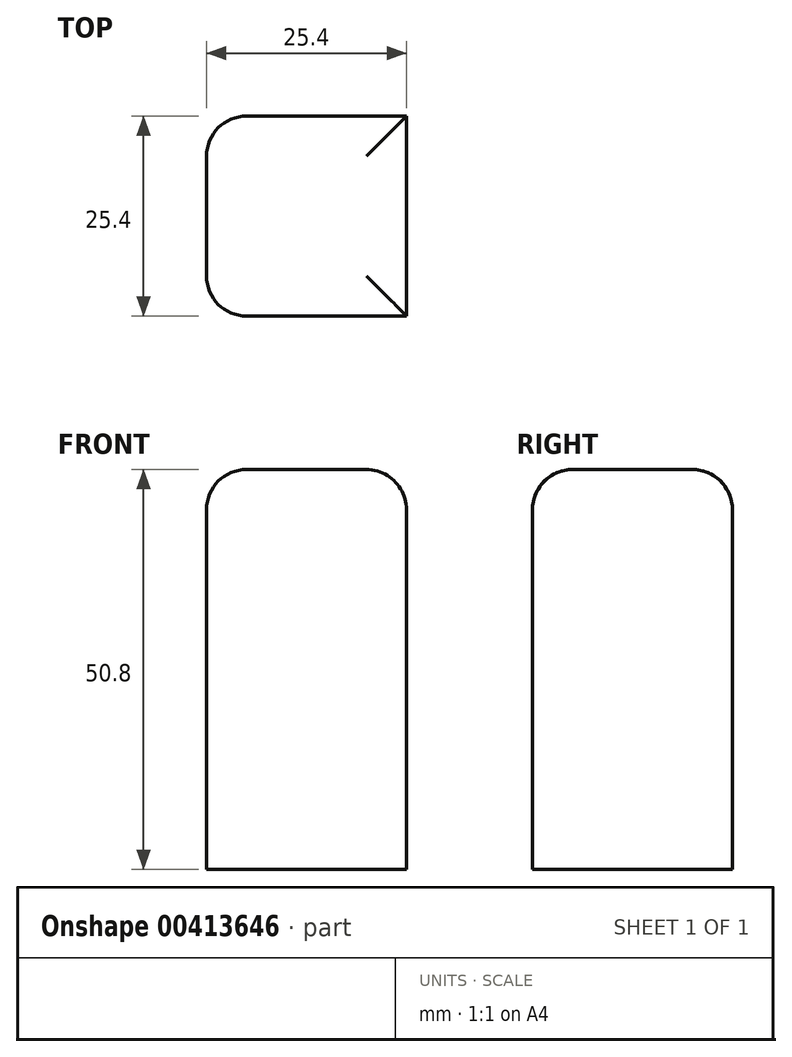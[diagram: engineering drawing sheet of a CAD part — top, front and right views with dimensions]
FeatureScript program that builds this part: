
annotation { "Feature Type Name" : "Feature", "Feature Type Description" : "" }
export const myFeature = defineFeature(function(context is Context, id is Id, definition is map)
    precondition{}
    {
        {
            var Q0;
            Q0=qCreatedBy(makeId("Top.planeOp"),FACE);
            var sketch = newSketch(context, id + "F0", { "sketchPlane" : qUnion([Q0])});
            skLineSegment(sketch, "E0.bottom", {"start": v(-47.8, -39.45) * mm, "end": v(-22.4, -39.45) * mm});
            skLineSegment(sketch, "E0.top", {"start": v(-47.8, -14.05) * mm, "end": v(-22.4, -14.05) * mm});
            skLineSegment(sketch, "E0.left", {"start": v(-47.8, -39.45) * mm, "end": v(-47.8, -14.05) * mm});
            skLineSegment(sketch, "E0.right", {"start": v(-22.4, -39.45) * mm, "end": v(-22.4, -14.05) * mm});
            skSolve(sketch);
        }
        {
            var Q0;
            Q0 = qSketchRegion(id + "F0", true);
            extrude(context, id + "F1", {"entities" : qUnion([Q0]), "depth" : 50.8 * mm});
        }
        {
            var Q0;
            Q0=makeQuery(id+"F1.opExtrude","CAP_EDGE",EDGE,{"disambiguationData":[OSD([sQuery(id+"F0.wireOp",EDGE,"E0.left")])],"isStart":false});
            fillet(context, id + "F2", {"entities" : qUnion([Q0]), "radius" : 5.08 * mm, "tangentPropagation" : true, "allowEdgeOverflow" : false});
        }
        {
            var Q0;
            Q0=makeQuery(id+"F1.opExtrude","CAP_EDGE",EDGE,{"disambiguationData":[OSD([sQuery(id+"F0.wireOp",EDGE,"E0.bottom")])],"isStart":false});
            var Q1;
            Q1=makeQuery(id+"F1.opExtrude","CAP_EDGE",EDGE,{"disambiguationData":[OSD([sQuery(id+"F0.wireOp",EDGE,"E0.right")])],"isStart":false});
            var Q2;
            Q2=makeQuery(id+"F1.opExtrude","CAP_EDGE",EDGE,{"disambiguationData":[OSD([sQuery(id+"F0.wireOp",EDGE,"E0.top")])],"isStart":false});
            fillet(context, id + "F3", {"entities" : qUnion([Q0, Q1, Q2]), "radius" : 5.08 * mm, "tangentPropagation" : true, "allowEdgeOverflow" : false});
        }
    });
